# Revit family: skamya_bridget
name_source: partatom
category: Антураж
revit_build: Autodesk Revit 2017 (Build: 20160225_1515(x64)
units: mm (PartAtom-declared; Revit-internal decimal feet)

## family parameters
Всегда вертикально = Да
Источник визуального образа = Геометрия семейства
На основе рабочей плоскости = Нет
Общий = Нет
При загрузке вырезать с полостями = Нет
Точка расчета площади = Нет

## types (7) — shared parameters
Высота = 730 мм
Длина = 2000 мм
Материал настила = Настил
Материал профильной трубы = Сталь
Наименование = Скамья "Бриджет"
Объем бетона = 0.11 м³
Производитель = ГК Очаковский комбинат ЖБИ
Ширина = 420 мм

## per-type parameters (varying)
| type | URL | Материал |
| "Бриджет" Белый шелк |  | Очаковский_Белый_Шелк |
| "Бриджет" Крымский берег |  | Очаковский_Крымский_берег |
| "Бриджет" Московский гравий |  | Очаковский_Московский_гравий |
| "Бриджет" Морская соль |  | Очаковский_Морская_соль |
| "Бриджет" Черный шелк | http://file-system.ru | Очаковский_Черный_шелк |
| "Бриджет" Черный глянец |  | Очаковский_Черный_глянец |
| "Бриджет" Шахматка |  | Очаковский_Шахматка |

## geometry (parser evidence)
native form markers: Blend x149
no freeform markers — native parametric forms only
